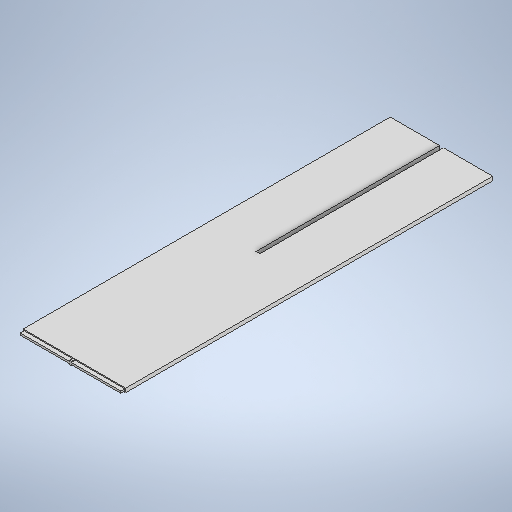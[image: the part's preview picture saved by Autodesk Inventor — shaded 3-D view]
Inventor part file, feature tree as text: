
AUTODESK INVENTOR PART (.ipt)
format: ipt  version: 2025.2 (Build 292293000, 293)  size: 345,600 bytes
history: native  units: mm
features: extrude x9, sketch x9, projected_geometry x1
ambient origin geometry x8: Origin, YZ Plane, XZ Plane, XY Plane, X Axis, Y Axis, Z Axis, Center Point
bodies: Solid1 (feature_tree)
feature tree (19):
  extrude  "Extrusion1"  Depth=447.675mm
  extrude  "Extrusion2"  Depth=4.7625mm TaperAngle=0.0deg
  extrude  "Extrusion3"  Depth=6.0mm
  extrude  "Extrusion4"  Depth=10.0mm TaperAngle=0.0deg
  extrude  "Extrusion5"  Depth=4.763mm
  extrude  "Extrusion6"  Depth=2.374mm
  extrude  "Extrusion7"  Depth=4.763mm
  extrude  "Extrusion8"  Depth=12.5mm
  extrude  "Extrusion9"  Depth=10.0mm TaperAngle=0.0deg
  sketch  "Sketch1"  dims[d0=50.0mm d1=447.675mm]
  sketch  "Sketch2"  dims[d2=4.7625mm d3=0.0mm d9=4.7625mm d10=0.0mm]
  sketch  "Sketch3"  dims[d11=25.0mm d13=6.0mm]
  sketch  "Sketch4"  dims[d14=6.0mm d15=10.0mm d16=0.0mm]
  projected_geometry  "Projected Loop1"
  sketch  "Sketch7"  dims[d17=158.838mm d18=0.0mm d20=4.763mm]
  sketch  "Sketch8"  dims[d21=223.837mm d22=0.0mm d25=2.374mm]
  sketch  "Sketch9"  dims[d26=4.763mm d27=0.0mm d28=25.0mm]
  sketch  "Sketch10"  dims[d29=10.0mm d30=0.0mm d31=12.5mm]
  sketch  "Sketch11"  dims[d32=10.0mm d33=0.0mm d37=10.0mm d38=0.0mm]
